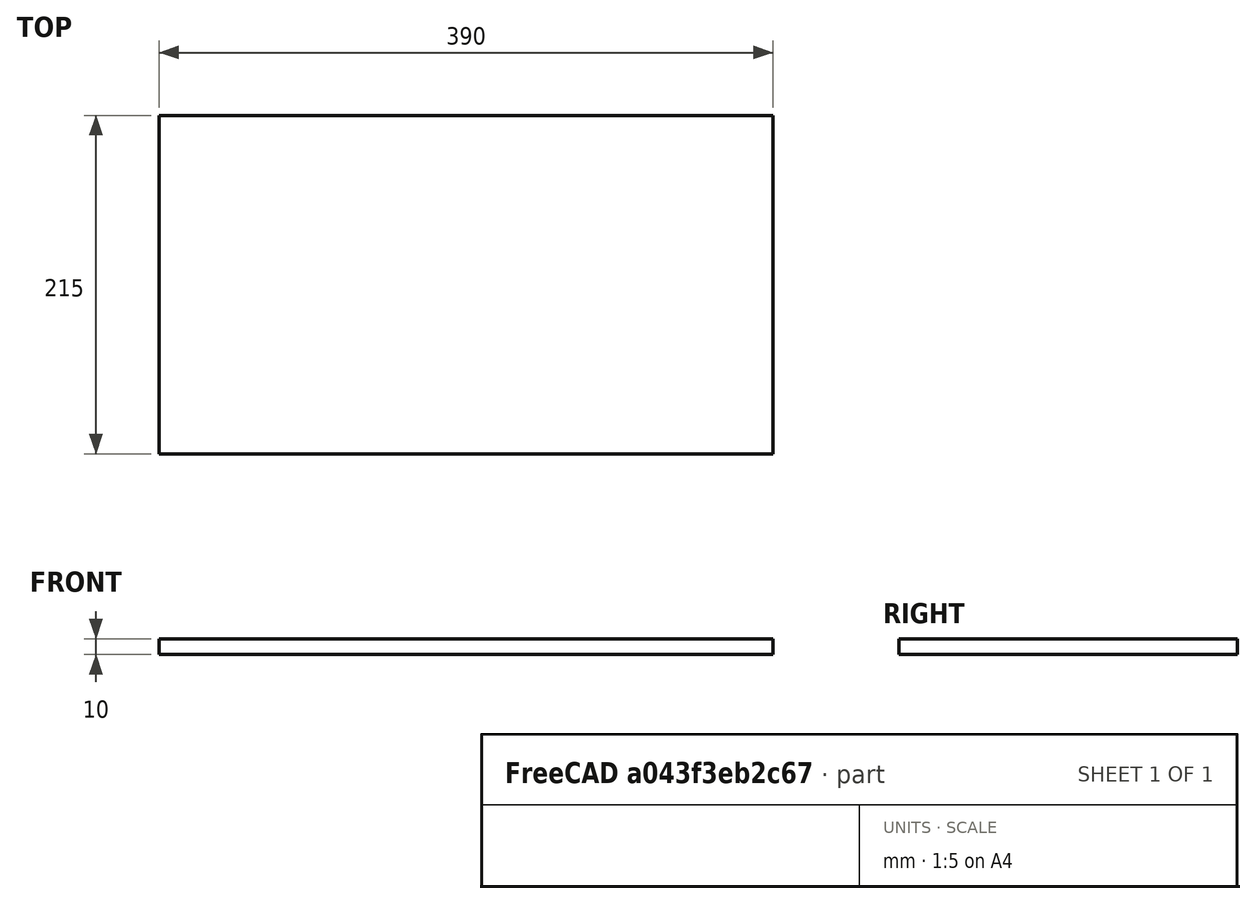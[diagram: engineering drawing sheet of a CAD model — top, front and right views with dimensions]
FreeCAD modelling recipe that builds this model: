
FCSTD DOCUMENT  (FreeCAD 0.18R4 (GitTag))
Label: BackBig
License: All rights reserved
LicenseURL: http://en.wikipedia.org/wiki/All_rights_reserved
objects: Sketcher::SketchObject×1, PartDesign::Pad×1, PartDesign::Body×1
note: 4 computed .brp shape members not serialized (recipe doc carries the construction recipe); baked Part::Feature solids carry a one-line shape summary decoded from their .brp

FEATURE [Sketcher::SketchObject] Sketch
  MapMode = 5
  Support = -> [XY_Plane]
  sketch-geometry (4):
    g0: LineSegment StartX=0 StartY=0 StartZ=0 EndX=-390 EndY=0 EndZ=0
    g1: LineSegment StartX=-390 StartY=0 StartZ=0 EndX=-390 EndY=215 EndZ=0
    g2: LineSegment StartX=-390 StartY=215 StartZ=0 EndX=0 EndY=215 EndZ=0
    g3: LineSegment StartX=0 StartY=215 StartZ=0 EndX=0 EndY=0 EndZ=0
  constraints (11):
    c: Coincident(g0,g1)
    c: Coincident(g1,g2)
    c: Coincident(g2,g3)
    c: Coincident(g3,g0)
    c: Horizontal(g0)
    c: Horizontal(g2)
    c: Vertical(g1)
    c: Vertical(g3)
    c: Distance(g2) = 390
    c: Distance(g3) = 215
    c: Coincident(g0,g-1)
FEATURE [PartDesign::Pad] Pad
  Length = 10
  Length2 = 100
  Profile = -> Sketch
  Type = 0
FEATURE [PartDesign::Body] Body
  Group = -> [Sketch,Pad]
  Origin = -> Origin
  Tip = -> Pad
